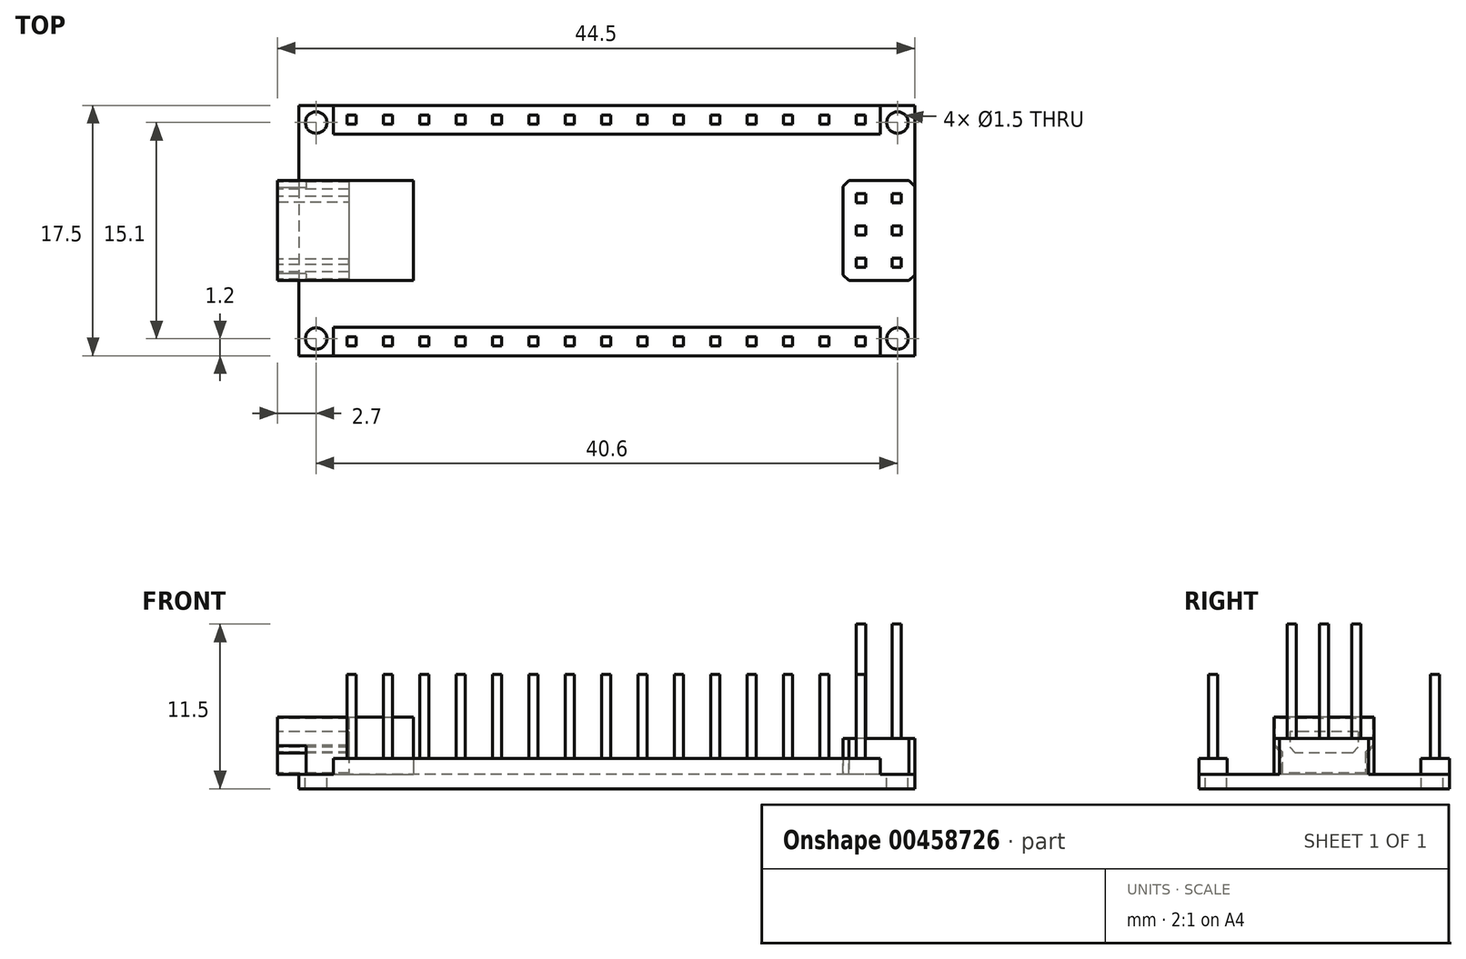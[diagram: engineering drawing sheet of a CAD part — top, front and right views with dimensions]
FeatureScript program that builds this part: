
annotation { "Feature Type Name" : "Feature", "Feature Type Description" : "" }
export const myFeature = defineFeature(function(context is Context, id is Id, definition is map)
    precondition{}
    {
        {
            var Q0;
            Q0=qCreatedBy(makeId("Top.planeOp"),FACE);
            var sketch = newSketch(context, id + "F0", { "sketchPlane" : qUnion([Q0])});
            skLineSegment(sketch, "E0.bottom", {"start": v(21.5, 8.75) * mm, "end": v(-21.5, 8.75) * mm});
            skLineSegment(sketch, "E0.top", {"start": v(21.5, -8.75) * mm, "end": v(-21.5, -8.75) * mm});
            skLineSegment(sketch, "E0.left", {"start": v(21.5, 8.75) * mm, "end": v(21.5, -8.75) * mm});
            skLineSegment(sketch, "E0.right", {"start": v(-21.5, 8.75) * mm, "end": v(-21.5, -8.75) * mm});
            skPoint(sketch, "E0.middle", {"position": v(0, 0) * mm});
            skCircle(sketch, "E1", {"center": v(-20.3, 7.55) * mm, "radius": 0.75 * mm});
            skCircle(sketch, "E2.0.1.0", {"center": v(-20.3, -7.55) * mm, "radius": 0.75 * mm});
            skCircle(sketch, "E2.1.0.0", {"center": v(20.3, 7.55) * mm, "radius": 0.75 * mm});
            skCircle(sketch, "E2.1.1.0", {"center": v(20.3, -7.55) * mm, "radius": 0.75 * mm});
            skLineSegment(sketch, "E2.direction1", {"start": v(-20.3, 7.55) * mm, "end": v(20.3, 7.55) * mm, "construction": true});
            skLineSegment(sketch, "E2.direction2", {"start": v(-20.3, 7.55) * mm, "end": v(-20.3, -7.55) * mm, "construction": true});
            skPoint(sketch, "E3", {"position": v(21.5, 0) * mm});
            skPoint(sketch, "E4", {"position": v(-21.5, 0) * mm});
            skLineSegment(sketch, "E5.bottom", {"start": v(-23, 3.5) * mm, "end": v(-13.5, 3.5) * mm});
            skLineSegment(sketch, "E5.top", {"start": v(-23, -3.5) * mm, "end": v(-13.5, -3.5) * mm});
            skLineSegment(sketch, "E5.left", {"start": v(-23, 3.5) * mm, "end": v(-23, -3.5) * mm});
            skLineSegment(sketch, "E5.right", {"start": v(-13.5, 3.5) * mm, "end": v(-13.5, -3.5) * mm});
            skPoint(sketch, "E6", {"position": v(-13.5, 0) * mm});
            skLineSegment(sketch, "E7.bottom", {"start": v(21.5, 3.5) * mm, "end": v(16.5, 3.5) * mm});
            skLineSegment(sketch, "E7.top", {"start": v(21.5, -3.5) * mm, "end": v(16.5, -3.5) * mm});
            skLineSegment(sketch, "E7.left", {"start": v(21.5, 3.5) * mm, "end": v(21.5, -3.5) * mm});
            skLineSegment(sketch, "E7.right", {"start": v(16.5, 3.5) * mm, "end": v(16.5, -3.5) * mm});
            skSolve(sketch);
        }
        {
            var Q0;
            {var subQ5=sQuery(id+"F0.wireOp",EDGE,"E5.right");Q0=makeQuery(id+"F0.imprint","IMPRINT",FACE,{"disambiguationData":[TD([[makeQuery(id+"F0.imprint","IMPRINT",EDGE,{"derivedFrom":subQ5}),-1.0]])]});}
            var Q1;
            {var subQ0=sQuery(id+"F0.wireOp",EDGE,"E0.bottom");Q1=makeQuery(id+"F0.imprint","IMPRINT",FACE,{"disambiguationData":[TD([[makeQuery(id+"F0.imprint","IMPRINT",EDGE,{"derivedFrom":subQ0}),1.0]])]});}
            var Q2;
            Q2=makeQuery(id+"F0.imprint","IMPRINT",FACE,{"disambiguationData":[TD([[makeQuery(id+"F0.imprint","IMPRINT",EDGE,{"derivedFrom":sQuery(id+"F0.wireOp",EDGE,"E7.bottom")}),1.0]])]});
            extrude(context, id + "F1", {"entities" : qUnion([Q0, Q1, Q2]), "oppositeDirection" : true, "depth" : 1 * mm});
        }
        {
            var Q0;
            {var subQ5=sQuery(id+"F0.wireOp",EDGE,"E5.left");Q0=makeQuery(id+"F0.imprint","IMPRINT",FACE,{"disambiguationData":[TD([[makeQuery(id+"F0.imprint","IMPRINT",EDGE,{"derivedFrom":subQ5}),1.0]])]});}
            var Q1;
            {var subQ5=sQuery(id+"F0.wireOp",EDGE,"E5.right");Q1=makeQuery(id+"F0.imprint","IMPRINT",FACE,{"disambiguationData":[TD([[makeQuery(id+"F0.imprint","IMPRINT",EDGE,{"derivedFrom":subQ5}),-1.0]])]});}
            extrude(context, id + "F2", {"entities" : qUnion([Q0, Q1]), "operationType" : NewBodyOperationType.ADD, "depth" : 4 * mm});
        }
        {
            var Q0;
            Q0=makeQuery(id+"F0.imprint","IMPRINT",FACE,{"disambiguationData":[TD([[makeQuery(id+"F0.imprint","IMPRINT",EDGE,{"derivedFrom":sQuery(id+"F0.wireOp",EDGE,"E7.bottom")}),1.0]])]});
            extrude(context, id + "F3", {"entities" : qUnion([Q0]), "operationType" : NewBodyOperationType.ADD, "depth" : 2.5 * mm});
        }
        {
            var Q0;
            Q0=makeQuery(id+"F2.opExtrude","SWEPT_FACE",FACE,{"disambiguationData":[OSD([sQuery(id+"F0.wireOp",EDGE,"E5.left")])]});
            var sketch = newSketch(context, id + "F4", { "sketchPlane" : qUnion([Q0])});
            skPoint(sketch, "E8", {"position": v(-3.5, 2) * mm});
            skPoint(sketch, "E9", {"position": v(3.5, 2) * mm});
            skPoint(sketch, "E10", {"position": v(-3, 0) * mm});
            skPoint(sketch, "E11", {"position": v(3, 0) * mm});
            skPoint(sketch, "E12", {"position": v(-3, 1.5) * mm});
            skPoint(sketch, "E13", {"position": v(3, 1.5) * mm});
            skLineSegment(sketch, "E14", {"start": v(-3.5, 2) * mm, "end": v(-3, 1.5) * mm});
            skLineSegment(sketch, "E15", {"start": v(-3, 0) * mm, "end": v(-3, 1.5) * mm});
            skLineSegment(sketch, "E16", {"start": v(3, 0) * mm, "end": v(3, 1.5) * mm});
            skLineSegment(sketch, "E17", {"start": v(3, 1.5) * mm, "end": v(3.5, 2) * mm});
            skLineSegment(sketch, "E18.bottom", {"start": v(-2.4, 3) * mm, "end": v(2.4, 3) * mm});
            skLineSegment(sketch, "E18.top", {"start": v(-2.4, 1.5) * mm, "end": v(2.4, 1.5) * mm});
            skLineSegment(sketch, "E18.left", {"start": v(-2.4, 3) * mm, "end": v(-2.4, 1.5) * mm});
            skLineSegment(sketch, "E18.right", {"start": v(2.4, 3) * mm, "end": v(2.4, 1.5) * mm});
            skPoint(sketch, "E19", {"position": v(0, 3) * mm});
            skPoint(sketch, "E20", {"position": v(-2.4, 2.25) * mm});
            skPoint(sketch, "E21", {"position": v(-3.5, 4) * mm});
            skPoint(sketch, "E22", {"position": v(3.5, 4) * mm});
            skLineSegment(sketch, "E23.0", {"start": v(-3.5, -1) * mm, "end": v(3.5, -1) * mm});
            skLineSegment(sketch, "E24", {"start": v(-3.5, 4) * mm, "end": v(-3.5, 2) * mm});
            skLineSegment(sketch, "E25", {"start": v(-3, 1.5) * mm, "end": v(-3, 0) * mm});
            skLineSegment(sketch, "E26", {"start": v(-3, 0) * mm, "end": v(3, 0) * mm});
            skLineSegment(sketch, "E27", {"start": v(3.5, 2) * mm, "end": v(3.5, 4) * mm});
            skLineSegment(sketch, "E28.0", {"start": v(-3.4, 3.9) * mm, "end": v(3.4, 3.9) * mm});
            skLineSegment(sketch, "E28.1", {"start": v(3.4, 2.04) * mm, "end": v(3.4, 3.9) * mm});
            skLineSegment(sketch, "E28.2", {"start": v(-3.4, 3.9) * mm, "end": v(-3.4, 2.04) * mm});
            skLineSegment(sketch, "E28.3", {"start": v(2.9, 1.54) * mm, "end": v(3.4, 2.04) * mm});
            skLineSegment(sketch, "E28.4", {"start": v(-3.4, 2.04) * mm, "end": v(-2.9, 1.54) * mm});
            skLineSegment(sketch, "E28.5", {"start": v(-2.9, 1.54) * mm, "end": v(-2.9, 0.1) * mm});
            skLineSegment(sketch, "E28.6", {"start": v(-2.9, 0.1) * mm, "end": v(2.9, 0.1) * mm});
            skLineSegment(sketch, "E28.7", {"start": v(2.9, 0.1) * mm, "end": v(2.9, 1.54) * mm});
            skPoint(sketch, "E29", {"position": v(-3.4, 2.04) * mm});
            skPoint(sketch, "E30", {"position": v(-2.9, 1.54) * mm});
            skSolve(sketch);
        }
        {
            var Q0;
            Q0=makeQuery(id+"F4.imprint","IMPRINT",FACE,{"disambiguationData":[TD([[makeQuery(id+"F4.imprint","IMPRINT",EDGE,{"derivedFrom":sQuery(id+"F4.wireOp",EDGE,"E18.bottom")}),1.0]])]});
            extrude(context, id + "F5", {"entities" : qUnion([Q0]), "operationType" : NewBodyOperationType.REMOVE, "oppositeDirection" : true, "depth" : 5 * mm});
        }
        {
            var Q0;
            {var subQ0=sQuery(id+"F4.wireOp",EDGE,"E14");Q0=makeQuery(id+"F4.imprint","IMPRINT",FACE,{"disambiguationData":[TD([[makeQuery(id+"F4.imprint","IMPRINT",EDGE,{"derivedFrom":subQ0}),-1.0]])]});}
            var Q1;
            {var subQ0=sQuery(id+"F4.wireOp",EDGE,"E16");Q1=makeQuery(id+"F4.imprint","IMPRINT",FACE,{"disambiguationData":[TD([[makeQuery(id+"F4.imprint","IMPRINT",EDGE,{"derivedFrom":subQ0}),-1.0]])]});}
            extrude(context, id + "F6", {"entities" : qUnion([Q0, Q1]), "operationType" : NewBodyOperationType.REMOVE, "oppositeDirection" : true, "depth" : 2 * mm});
        }
        {
            var Q0;
            Q0=makeQuery(id+"F1.opExtrude","CAP_FACE",FACE,{"disambiguationData":[OSD([sQuery(id+"F0.wireOp",EDGE,"E0.bottom"),sQuery(id+"F0.wireOp",EDGE,"E0.top"),sQuery(id+"F0.wireOp",EDGE,"E0.left"),sQuery(id+"F0.wireOp",EDGE,"E0.right"),sQuery(id+"F0.wireOp",EDGE,"E1"),sQuery(id+"F0.wireOp",EDGE,"E2.0.1.0"),sQuery(id+"F0.wireOp",EDGE,"E2.1.0.0"),sQuery(id+"F0.wireOp",EDGE,"E2.1.1.0"),sQuery(id+"F0.wireOp",EDGE,"E7.left")])],"isStart":false});
            var sketch = newSketch(context, id + "F7", { "sketchPlane" : qUnion([Q0])});
            skLineSegment(sketch, "E31.bottom", {"start": v(-19.1, 8.75) * mm, "end": v(19.1, 8.75) * mm});
            skLineSegment(sketch, "E31.top", {"start": v(-19.1, 6.75) * mm, "end": v(19.1, 6.75) * mm});
            skLineSegment(sketch, "E31.left", {"start": v(-19.1, 8.75) * mm, "end": v(-19.1, 6.75) * mm});
            skLineSegment(sketch, "E31.right", {"start": v(19.1, 8.75) * mm, "end": v(19.1, 6.75) * mm});
            skPoint(sketch, "E32", {"position": v(0, 6.75) * mm});
            skLineSegment(sketch, "E33", {"start": v(-19.1, 7.75) * mm, "end": v(19.1, 7.75) * mm, "construction": true});
            skPoint(sketch, "E34", {"position": v(-17.83, 7.75) * mm});
            skLineSegment(sketch, "E35.bottom", {"start": v(-17.51, 8.07) * mm, "end": v(-18.15, 8.07) * mm});
            skLineSegment(sketch, "E35.top", {"start": v(-17.51, 7.43) * mm, "end": v(-18.15, 7.43) * mm});
            skLineSegment(sketch, "E35.left", {"start": v(-17.51, 8.07) * mm, "end": v(-17.51, 7.43) * mm});
            skLineSegment(sketch, "E35.right", {"start": v(-18.15, 8.07) * mm, "end": v(-18.15, 7.43) * mm});
            skPoint(sketch, "E36.1.0.0", {"position": v(-15.3, 7.75) * mm});
            skLineSegment(sketch, "E36.1.0.1", {"start": v(-14.97, 8.07) * mm, "end": v(-14.97, 7.43) * mm});
            skLineSegment(sketch, "E36.1.0.2", {"start": v(-14.97, 8.07) * mm, "end": v(-15.61, 8.07) * mm});
            skLineSegment(sketch, "E36.1.0.3", {"start": v(-15.61, 8.07) * mm, "end": v(-15.61, 7.43) * mm});
            skLineSegment(sketch, "E36.1.0.4", {"start": v(-14.97, 7.43) * mm, "end": v(-15.61, 7.43) * mm});
            skPoint(sketch, "E36.2.0.0", {"position": v(-12.75, 7.75) * mm});
            skLineSegment(sketch, "E36.2.0.1", {"start": v(-12.43, 8.07) * mm, "end": v(-12.43, 7.43) * mm});
            skLineSegment(sketch, "E36.2.0.2", {"start": v(-12.43, 8.07) * mm, "end": v(-13.07, 8.07) * mm});
            skLineSegment(sketch, "E36.2.0.3", {"start": v(-13.07, 8.07) * mm, "end": v(-13.07, 7.43) * mm});
            skLineSegment(sketch, "E36.2.0.4", {"start": v(-12.43, 7.43) * mm, "end": v(-13.07, 7.43) * mm});
            skPoint(sketch, "E36.3.0.0", {"position": v(-10.21, 7.75) * mm});
            skLineSegment(sketch, "E36.3.0.1", {"start": v(-9.89, 8.07) * mm, "end": v(-9.89, 7.43) * mm});
            skLineSegment(sketch, "E36.3.0.2", {"start": v(-9.89, 8.07) * mm, "end": v(-10.53, 8.07) * mm});
            skLineSegment(sketch, "E36.3.0.3", {"start": v(-10.53, 8.07) * mm, "end": v(-10.53, 7.43) * mm});
            skLineSegment(sketch, "E36.3.0.4", {"start": v(-9.89, 7.43) * mm, "end": v(-10.53, 7.43) * mm});
            skPoint(sketch, "E36.4.0.0", {"position": v(-7.67, 7.75) * mm});
            skLineSegment(sketch, "E36.4.0.1", {"start": v(-7.35, 8.07) * mm, "end": v(-7.35, 7.43) * mm});
            skLineSegment(sketch, "E36.4.0.2", {"start": v(-7.35, 8.07) * mm, "end": v(-8, 8.07) * mm});
            skLineSegment(sketch, "E36.4.0.3", {"start": v(-8, 8.07) * mm, "end": v(-8, 7.43) * mm});
            skLineSegment(sketch, "E36.4.0.4", {"start": v(-7.35, 7.43) * mm, "end": v(-8, 7.43) * mm});
            skPoint(sketch, "E36.5.0.0", {"position": v(-5.13, 7.75) * mm});
            skLineSegment(sketch, "E36.5.0.1", {"start": v(-4.8, 8.07) * mm, "end": v(-4.8, 7.43) * mm});
            skLineSegment(sketch, "E36.5.0.2", {"start": v(-4.8, 8.07) * mm, "end": v(-5.45, 8.07) * mm});
            skLineSegment(sketch, "E36.5.0.3", {"start": v(-5.45, 8.07) * mm, "end": v(-5.45, 7.43) * mm});
            skLineSegment(sketch, "E36.5.0.4", {"start": v(-4.8, 7.43) * mm, "end": v(-5.45, 7.43) * mm});
            skPoint(sketch, "E36.6.0.0", {"position": v(-2.59, 7.75) * mm});
            skLineSegment(sketch, "E36.6.0.1", {"start": v(-2.27, 8.07) * mm, "end": v(-2.27, 7.43) * mm});
            skLineSegment(sketch, "E36.6.0.2", {"start": v(-2.27, 8.07) * mm, "end": v(-2.9, 8.07) * mm});
            skLineSegment(sketch, "E36.6.0.3", {"start": v(-2.9, 8.07) * mm, "end": v(-2.9, 7.43) * mm});
            skLineSegment(sketch, "E36.6.0.4", {"start": v(-2.27, 7.43) * mm, "end": v(-2.9, 7.43) * mm});
            skPoint(sketch, "E36.7.0.0", {"position": v(-0.05, 7.75) * mm});
            skLineSegment(sketch, "E36.7.0.1", {"start": v(0.27, 8.07) * mm, "end": v(0.27, 7.43) * mm});
            skLineSegment(sketch, "E36.7.0.2", {"start": v(0.27, 8.07) * mm, "end": v(-0.37, 8.07) * mm});
            skLineSegment(sketch, "E36.7.0.3", {"start": v(-0.37, 8.07) * mm, "end": v(-0.37, 7.43) * mm});
            skLineSegment(sketch, "E36.7.0.4", {"start": v(0.27, 7.43) * mm, "end": v(-0.37, 7.43) * mm});
            skPoint(sketch, "E36.8.0.0", {"position": v(2.5, 7.75) * mm});
            skLineSegment(sketch, "E36.8.0.1", {"start": v(2.81, 8.07) * mm, "end": v(2.81, 7.43) * mm});
            skLineSegment(sketch, "E36.8.0.2", {"start": v(2.81, 8.07) * mm, "end": v(2.17, 8.07) * mm});
            skLineSegment(sketch, "E36.8.0.3", {"start": v(2.17, 8.07) * mm, "end": v(2.17, 7.43) * mm});
            skLineSegment(sketch, "E36.8.0.4", {"start": v(2.81, 7.43) * mm, "end": v(2.17, 7.43) * mm});
            skPoint(sketch, "E36.9.0.0", {"position": v(5.03, 7.75) * mm});
            skLineSegment(sketch, "E36.9.0.1", {"start": v(5.35, 8.07) * mm, "end": v(5.35, 7.43) * mm});
            skLineSegment(sketch, "E36.9.0.2", {"start": v(5.35, 8.07) * mm, "end": v(4.71, 8.07) * mm});
            skLineSegment(sketch, "E36.9.0.3", {"start": v(4.71, 8.07) * mm, "end": v(4.71, 7.43) * mm});
            skLineSegment(sketch, "E36.9.0.4", {"start": v(5.35, 7.43) * mm, "end": v(4.71, 7.43) * mm});
            skPoint(sketch, "E36.10.0.0", {"position": v(7.57, 7.75) * mm});
            skLineSegment(sketch, "E36.10.0.1", {"start": v(7.9, 8.07) * mm, "end": v(7.9, 7.43) * mm});
            skLineSegment(sketch, "E36.10.0.2", {"start": v(7.9, 8.07) * mm, "end": v(7.25, 8.07) * mm});
            skLineSegment(sketch, "E36.10.0.3", {"start": v(7.25, 8.07) * mm, "end": v(7.25, 7.43) * mm});
            skLineSegment(sketch, "E36.10.0.4", {"start": v(7.9, 7.43) * mm, "end": v(7.25, 7.43) * mm});
            skPoint(sketch, "E36.11.0.0", {"position": v(10.11, 7.75) * mm});
            skLineSegment(sketch, "E36.11.0.1", {"start": v(10.43, 8.07) * mm, "end": v(10.43, 7.43) * mm});
            skLineSegment(sketch, "E36.11.0.2", {"start": v(10.43, 8.07) * mm, "end": v(9.8, 8.07) * mm});
            skLineSegment(sketch, "E36.11.0.3", {"start": v(9.8, 8.07) * mm, "end": v(9.8, 7.43) * mm});
            skLineSegment(sketch, "E36.11.0.4", {"start": v(10.43, 7.43) * mm, "end": v(9.8, 7.43) * mm});
            skPoint(sketch, "E36.12.0.0", {"position": v(12.65, 7.75) * mm});
            skLineSegment(sketch, "E36.12.0.1", {"start": v(12.97, 8.07) * mm, "end": v(12.97, 7.43) * mm});
            skLineSegment(sketch, "E36.12.0.2", {"start": v(12.97, 8.07) * mm, "end": v(12.33, 8.07) * mm});
            skLineSegment(sketch, "E36.12.0.3", {"start": v(12.33, 8.07) * mm, "end": v(12.33, 7.43) * mm});
            skLineSegment(sketch, "E36.12.0.4", {"start": v(12.97, 7.43) * mm, "end": v(12.33, 7.43) * mm});
            skPoint(sketch, "E36.13.0.0", {"position": v(15.2, 7.75) * mm});
            skLineSegment(sketch, "E36.13.0.1", {"start": v(15.51, 8.07) * mm, "end": v(15.51, 7.43) * mm});
            skLineSegment(sketch, "E36.13.0.2", {"start": v(15.51, 8.07) * mm, "end": v(14.87, 8.07) * mm});
            skLineSegment(sketch, "E36.13.0.3", {"start": v(14.87, 8.07) * mm, "end": v(14.87, 7.43) * mm});
            skLineSegment(sketch, "E36.13.0.4", {"start": v(15.51, 7.43) * mm, "end": v(14.87, 7.43) * mm});
            skPoint(sketch, "E36.14.0.0", {"position": v(17.73, 7.75) * mm});
            skLineSegment(sketch, "E36.14.0.1", {"start": v(18.05, 8.07) * mm, "end": v(18.05, 7.43) * mm});
            skLineSegment(sketch, "E36.14.0.2", {"start": v(18.05, 8.07) * mm, "end": v(17.41, 8.07) * mm});
            skLineSegment(sketch, "E36.14.0.3", {"start": v(17.41, 8.07) * mm, "end": v(17.41, 7.43) * mm});
            skLineSegment(sketch, "E36.14.0.4", {"start": v(18.05, 7.43) * mm, "end": v(17.41, 7.43) * mm});
            skLineSegment(sketch, "E36.direction1", {"start": v(-17.83, 7.75) * mm, "end": v(-15.3, 7.75) * mm, "construction": true});
            skPoint(sketch, "E37", {"position": v(-20.3, 7.55) * mm});
            skLineSegment(sketch, "E38", {"start": v(-20.3, 7.55) * mm, "end": v(-21.5, 7.55) * mm});
            skLineSegment(sketch, "E39", {"start": v(-21.5, 7.55) * mm, "end": v(-19.1, 7.55) * mm});
            skPoint(sketch, "E40", {"position": v(-21.05, 7.55) * mm});
            skPoint(sketch, "E41", {"position": v(-19.55, 7.55) * mm});
            skPoint(sketch, "E42", {"position": v(20.3, 7.55) * mm});
            skLineSegment(sketch, "E43", {"start": v(20.3, 7.55) * mm, "end": v(21.5, 7.55) * mm});
            skLineSegment(sketch, "E44", {"start": v(21.5, 7.55) * mm, "end": v(19.1, 7.55) * mm});
            skPoint(sketch, "E45", {"position": v(21.05, 7.55) * mm});
            skPoint(sketch, "E46", {"position": v(19.55, 7.55) * mm});
            skPoint(sketch, "E47.0.1.0", {"position": v(-0.05, -7.75) * mm});
            skPoint(sketch, "E47.0.1.1", {"position": v(-5.13, -7.75) * mm});
            skPoint(sketch, "E47.0.1.2", {"position": v(12.65, -7.75) * mm});
            skPoint(sketch, "E47.0.1.3", {"position": v(-7.67, -7.75) * mm});
            skPoint(sketch, "E47.0.1.4", {"position": v(17.73, -7.75) * mm});
            skPoint(sketch, "E47.0.1.5", {"position": v(-10.21, -7.75) * mm});
            skPoint(sketch, "E47.0.1.6", {"position": v(7.57, -7.75) * mm});
            skPoint(sketch, "E47.0.1.7", {"position": v(2.49, -7.75) * mm});
            skPoint(sketch, "E47.0.1.8", {"position": v(0, -8.75) * mm});
            skPoint(sketch, "E47.0.1.9", {"position": v(-17.83, -7.75) * mm});
            skPoint(sketch, "E47.0.1.10", {"position": v(5.03, -7.75) * mm});
            skPoint(sketch, "E47.0.1.11", {"position": v(-15.3, -7.75) * mm});
            skLineSegment(sketch, "E47.0.1.12", {"start": v(-17.83, -7.75) * mm, "end": v(-15.3, -7.75) * mm, "construction": true});
            skPoint(sketch, "E47.0.1.13", {"position": v(10.11, -7.75) * mm});
            skPoint(sketch, "E47.0.1.14", {"position": v(15.2, -7.75) * mm});
            skPoint(sketch, "E47.0.1.15", {"position": v(-2.6, -7.75) * mm});
            skPoint(sketch, "E47.0.1.16", {"position": v(-12.75, -7.75) * mm});
            skPoint(sketch, "E47.0.1.17", {"position": v(-17.83, -7.75) * mm});
            skLineSegment(sketch, "E47.0.1.18", {"start": v(18.05, -7.43) * mm, "end": v(17.41, -7.43) * mm});
            skLineSegment(sketch, "E47.0.1.19", {"start": v(18.05, -8.07) * mm, "end": v(17.41, -8.07) * mm});
            skLineSegment(sketch, "E47.0.1.20", {"start": v(18.05, -7.43) * mm, "end": v(18.05, -8.07) * mm});
            skLineSegment(sketch, "E47.0.1.21", {"start": v(-0.37, -7.43) * mm, "end": v(-0.37, -8.07) * mm});
            skLineSegment(sketch, "E47.0.1.22", {"start": v(-10.53, -7.43) * mm, "end": v(-10.53, -8.07) * mm});
            skLineSegment(sketch, "E47.0.1.23", {"start": v(-9.89, -7.43) * mm, "end": v(-10.53, -7.43) * mm});
            skLineSegment(sketch, "E47.0.1.24", {"start": v(-2.27, -7.43) * mm, "end": v(-2.9, -7.43) * mm});
            skLineSegment(sketch, "E47.0.1.25", {"start": v(12.97, -7.43) * mm, "end": v(12.97, -8.07) * mm});
            skLineSegment(sketch, "E47.0.1.26", {"start": v(-5.45, -7.43) * mm, "end": v(-5.45, -8.07) * mm});
            skLineSegment(sketch, "E47.0.1.27", {"start": v(-7.35, -8.07) * mm, "end": v(-7.99, -8.07) * mm});
            skLineSegment(sketch, "E47.0.1.28", {"start": v(2.81, -8.07) * mm, "end": v(2.17, -8.07) * mm});
            skLineSegment(sketch, "E47.0.1.29", {"start": v(12.97, -8.07) * mm, "end": v(12.33, -8.07) * mm});
            skLineSegment(sketch, "E47.0.1.30", {"start": v(7.9, -8.07) * mm, "end": v(7.25, -8.07) * mm});
            skLineSegment(sketch, "E47.0.1.31", {"start": v(7.25, -7.43) * mm, "end": v(7.25, -8.07) * mm});
            skLineSegment(sketch, "E47.0.1.32", {"start": v(-2.9, -7.43) * mm, "end": v(-2.9, -8.07) * mm});
            skLineSegment(sketch, "E47.0.1.33", {"start": v(-7.35, -7.43) * mm, "end": v(-7.99, -7.43) * mm});
            skLineSegment(sketch, "E47.0.1.34", {"start": v(2.81, -7.43) * mm, "end": v(2.81, -8.07) * mm});
            skLineSegment(sketch, "E47.0.1.35", {"start": v(7.9, -7.43) * mm, "end": v(7.25, -7.43) * mm});
            skLineSegment(sketch, "E47.0.1.36", {"start": v(-4.8, -8.07) * mm, "end": v(-5.45, -8.07) * mm});
            skLineSegment(sketch, "E47.0.1.37", {"start": v(-7.35, -7.43) * mm, "end": v(-7.35, -8.07) * mm});
            skLineSegment(sketch, "E47.0.1.38", {"start": v(15.5, -8.07) * mm, "end": v(14.87, -8.07) * mm});
            skLineSegment(sketch, "E47.0.1.39", {"start": v(5.35, -8.07) * mm, "end": v(4.71, -8.07) * mm});
            skLineSegment(sketch, "E47.0.1.40", {"start": v(-2.27, -8.07) * mm, "end": v(-2.9, -8.07) * mm});
            skLineSegment(sketch, "E47.0.1.41", {"start": v(-12.43, -8.07) * mm, "end": v(-13.07, -8.07) * mm});
            skLineSegment(sketch, "E47.0.1.42", {"start": v(2.81, -7.43) * mm, "end": v(2.17, -7.43) * mm});
            skLineSegment(sketch, "E47.0.1.43", {"start": v(17.41, -7.43) * mm, "end": v(17.41, -8.07) * mm});
            skLineSegment(sketch, "E47.0.1.44", {"start": v(12.97, -7.43) * mm, "end": v(12.33, -7.43) * mm});
            skLineSegment(sketch, "E47.0.1.45", {"start": v(7.9, -7.43) * mm, "end": v(7.9, -8.07) * mm});
            skLineSegment(sketch, "E47.0.1.46", {"start": v(-2.27, -7.43) * mm, "end": v(-2.27, -8.07) * mm});
            skLineSegment(sketch, "E47.0.1.47", {"start": v(-17.5, -8.07) * mm, "end": v(-18.15, -8.07) * mm});
            skLineSegment(sketch, "E47.0.1.48", {"start": v(12.33, -7.43) * mm, "end": v(12.33, -8.07) * mm});
            skLineSegment(sketch, "E47.0.1.49", {"start": v(-14.97, -7.43) * mm, "end": v(-14.97, -8.07) * mm});
            skLineSegment(sketch, "E47.0.1.50", {"start": v(2.17, -7.43) * mm, "end": v(2.17, -8.07) * mm});
            skLineSegment(sketch, "E47.0.1.51", {"start": v(-8, -7.43) * mm, "end": v(-8, -8.07) * mm});
            skLineSegment(sketch, "E47.0.1.52", {"start": v(-14.97, -7.43) * mm, "end": v(-15.6, -7.43) * mm});
            skLineSegment(sketch, "E47.0.1.53", {"start": v(-15.61, -7.43) * mm, "end": v(-15.61, -8.07) * mm});
            skLineSegment(sketch, "E47.0.1.54", {"start": v(-14.97, -8.07) * mm, "end": v(-15.6, -8.07) * mm});
            skLineSegment(sketch, "E47.0.1.55", {"start": v(-9.89, -7.43) * mm, "end": v(-9.89, -8.07) * mm});
            skLineSegment(sketch, "E47.0.1.56", {"start": v(0.27, -7.43) * mm, "end": v(0.27, -8.07) * mm});
            skLineSegment(sketch, "E47.0.1.57", {"start": v(10.43, -7.43) * mm, "end": v(10.43, -8.07) * mm});
            skLineSegment(sketch, "E47.0.1.58", {"start": v(-12.43, -7.43) * mm, "end": v(-12.43, -8.07) * mm});
            skLineSegment(sketch, "E47.0.1.59", {"start": v(10.43, -7.43) * mm, "end": v(9.8, -7.43) * mm});
            skLineSegment(sketch, "E47.0.1.60", {"start": v(0.27, -7.43) * mm, "end": v(-0.37, -7.43) * mm});
            skLineSegment(sketch, "E47.0.1.61", {"start": v(15.51, -7.43) * mm, "end": v(15.51, -8.07) * mm});
            skLineSegment(sketch, "E47.0.1.62", {"start": v(5.35, -7.43) * mm, "end": v(5.35, -8.07) * mm});
            skLineSegment(sketch, "E47.0.1.63", {"start": v(-4.8, -7.43) * mm, "end": v(-4.8, -8.07) * mm});
            skLineSegment(sketch, "E47.0.1.64", {"start": v(15.51, -7.43) * mm, "end": v(14.87, -7.43) * mm});
            skLineSegment(sketch, "E47.0.1.65", {"start": v(5.35, -7.43) * mm, "end": v(4.71, -7.43) * mm});
            skLineSegment(sketch, "E47.0.1.66", {"start": v(-4.8, -7.43) * mm, "end": v(-5.45, -7.43) * mm});
            skLineSegment(sketch, "E47.0.1.67", {"start": v(10.43, -8.07) * mm, "end": v(9.8, -8.07) * mm});
            skLineSegment(sketch, "E47.0.1.68", {"start": v(0.27, -8.07) * mm, "end": v(-0.37, -8.07) * mm});
            skLineSegment(sketch, "E47.0.1.69", {"start": v(-9.9, -8.07) * mm, "end": v(-10.53, -8.07) * mm});
            skLineSegment(sketch, "E47.0.1.70", {"start": v(4.71, -7.43) * mm, "end": v(4.71, -8.07) * mm});
            skLineSegment(sketch, "E47.0.1.71", {"start": v(14.87, -7.43) * mm, "end": v(14.87, -8.07) * mm});
            skLineSegment(sketch, "E47.0.1.72", {"start": v(9.8, -7.43) * mm, "end": v(9.8, -8.07) * mm});
            skLineSegment(sketch, "E47.0.1.73", {"start": v(-12.43, -7.43) * mm, "end": v(-13.07, -7.43) * mm});
            skLineSegment(sketch, "E47.0.1.74", {"start": v(-13.07, -7.43) * mm, "end": v(-13.07, -8.07) * mm});
            skLineSegment(sketch, "E47.0.1.75", {"start": v(-18.15, -7.43) * mm, "end": v(-18.15, -8.07) * mm});
            skLineSegment(sketch, "E47.0.1.76", {"start": v(-17.51, -7.43) * mm, "end": v(-17.51, -8.07) * mm});
            skLineSegment(sketch, "E47.0.1.77", {"start": v(-17.5, -7.43) * mm, "end": v(-18.15, -7.43) * mm});
            skLineSegment(sketch, "E47.0.1.78", {"start": v(19.1, -6.75) * mm, "end": v(19.1, -8.75) * mm});
            skLineSegment(sketch, "E47.0.1.79", {"start": v(-19.1, -8.75) * mm, "end": v(19.1, -8.75) * mm});
            skLineSegment(sketch, "E47.0.1.80", {"start": v(-19.1, -6.75) * mm, "end": v(-19.1, -8.75) * mm});
            skLineSegment(sketch, "E47.0.1.81", {"start": v(-19.1, -6.75) * mm, "end": v(19.1, -6.75) * mm});
            skLineSegment(sketch, "E47.direction1", {"start": v(-0.05, 7.75) * mm, "end": v(24.95, 7.75) * mm, "construction": true});
            skLineSegment(sketch, "E47.direction2", {"start": v(-0.05, 7.75) * mm, "end": v(-0.05, -7.75) * mm, "construction": true});
            skSolve(sketch);
        }
        {
            var Q0;
            Q0=makeQuery(id+"F7.imprint","IMPRINT",FACE,{"disambiguationData":[TD([[makeQuery(id+"F7.imprint","IMPRINT",EDGE,{"derivedFrom":sQuery(id+"F7.wireOp",EDGE,"E47.0.1.18")}),-1.0]])]});
            var Q1;
            {var subQ1=sQuery(id+"F7.wireOp",EDGE,"E31.bottom");Q1=makeQuery(id+"F7.imprint","IMPRINT",FACE,{"disambiguationData":[TD([[makeQuery(id+"F7.imprint","IMPRINT",EDGE,{"derivedFrom":subQ1}),1.0]])]});}
            extrude(context, id + "F8", {"entities" : qUnion([Q0, Q1]), "oppositeDirection" : true, "depth" : 2.1 * mm, "offsetDistance" : 25 * mm});
        }
        {
            var Q0;
            Q0=makeQuery(id+"F7.imprint","IMPRINT",FACE,{"disambiguationData":[TD([[makeQuery(id+"F7.imprint","IMPRINT",EDGE,{"derivedFrom":sQuery(id+"F7.wireOp",EDGE,"E35.bottom")}),1.0]])]});
            var Q1;
            Q1=makeQuery(id+"F7.imprint","IMPRINT",FACE,{"disambiguationData":[TD([[makeQuery(id+"F7.imprint","IMPRINT",EDGE,{"derivedFrom":sQuery(id+"F7.wireOp",EDGE,"E36.1.0.1")}),-1.0]])]});
            var Q2;
            Q2=makeQuery(id+"F7.imprint","IMPRINT",FACE,{"disambiguationData":[TD([[makeQuery(id+"F7.imprint","IMPRINT",EDGE,{"derivedFrom":sQuery(id+"F7.wireOp",EDGE,"E36.2.0.1")}),-1.0]])]});
            var Q3;
            Q3=makeQuery(id+"F7.imprint","IMPRINT",FACE,{"disambiguationData":[TD([[makeQuery(id+"F7.imprint","IMPRINT",EDGE,{"derivedFrom":sQuery(id+"F7.wireOp",EDGE,"E36.3.0.1")}),-1.0]])]});
            var Q4;
            Q4=makeQuery(id+"F7.imprint","IMPRINT",FACE,{"disambiguationData":[TD([[makeQuery(id+"F7.imprint","IMPRINT",EDGE,{"derivedFrom":sQuery(id+"F7.wireOp",EDGE,"E36.4.0.1")}),-1.0]])]});
            var Q5;
            Q5=makeQuery(id+"F7.imprint","IMPRINT",FACE,{"disambiguationData":[TD([[makeQuery(id+"F7.imprint","IMPRINT",EDGE,{"derivedFrom":sQuery(id+"F7.wireOp",EDGE,"E36.5.0.1")}),-1.0]])]});
            var Q6;
            Q6=makeQuery(id+"F7.imprint","IMPRINT",FACE,{"disambiguationData":[TD([[makeQuery(id+"F7.imprint","IMPRINT",EDGE,{"derivedFrom":sQuery(id+"F7.wireOp",EDGE,"E36.6.0.1")}),-1.0]])]});
            var Q7;
            Q7=makeQuery(id+"F7.imprint","IMPRINT",FACE,{"disambiguationData":[TD([[makeQuery(id+"F7.imprint","IMPRINT",EDGE,{"derivedFrom":sQuery(id+"F7.wireOp",EDGE,"E36.7.0.1")}),-1.0]])]});
            var Q8;
            Q8=makeQuery(id+"F7.imprint","IMPRINT",FACE,{"disambiguationData":[TD([[makeQuery(id+"F7.imprint","IMPRINT",EDGE,{"derivedFrom":sQuery(id+"F7.wireOp",EDGE,"E36.8.0.1")}),-1.0]])]});
            var Q9;
            Q9=makeQuery(id+"F7.imprint","IMPRINT",FACE,{"disambiguationData":[TD([[makeQuery(id+"F7.imprint","IMPRINT",EDGE,{"derivedFrom":sQuery(id+"F7.wireOp",EDGE,"E36.9.0.1")}),-1.0]])]});
            var Q10;
            Q10=makeQuery(id+"F7.imprint","IMPRINT",FACE,{"disambiguationData":[TD([[makeQuery(id+"F7.imprint","IMPRINT",EDGE,{"derivedFrom":sQuery(id+"F7.wireOp",EDGE,"E36.10.0.1")}),-1.0]])]});
            var Q11;
            Q11=makeQuery(id+"F7.imprint","IMPRINT",FACE,{"disambiguationData":[TD([[makeQuery(id+"F7.imprint","IMPRINT",EDGE,{"derivedFrom":sQuery(id+"F7.wireOp",EDGE,"E36.11.0.1")}),-1.0]])]});
            var Q12;
            Q12=makeQuery(id+"F7.imprint","IMPRINT",FACE,{"disambiguationData":[TD([[makeQuery(id+"F7.imprint","IMPRINT",EDGE,{"derivedFrom":sQuery(id+"F7.wireOp",EDGE,"E36.12.0.1")}),-1.0]])]});
            var Q13;
            Q13=makeQuery(id+"F7.imprint","IMPRINT",FACE,{"disambiguationData":[TD([[makeQuery(id+"F7.imprint","IMPRINT",EDGE,{"derivedFrom":sQuery(id+"F7.wireOp",EDGE,"E36.13.0.1")}),-1.0]])]});
            var Q14;
            Q14=makeQuery(id+"F7.imprint","IMPRINT",FACE,{"disambiguationData":[TD([[makeQuery(id+"F7.imprint","IMPRINT",EDGE,{"derivedFrom":sQuery(id+"F7.wireOp",EDGE,"E36.14.0.1")}),-1.0]])]});
            var Q15;
            Q15=makeQuery(id+"F7.imprint","IMPRINT",FACE,{"disambiguationData":[TD([[makeQuery(id+"F7.imprint","IMPRINT",EDGE,{"derivedFrom":sQuery(id+"F7.wireOp",EDGE,"E47.0.1.47")}),-1.0]])]});
            var Q16;
            Q16=makeQuery(id+"F7.imprint","IMPRINT",FACE,{"disambiguationData":[TD([[makeQuery(id+"F7.imprint","IMPRINT",EDGE,{"derivedFrom":sQuery(id+"F7.wireOp",EDGE,"E47.0.1.49")}),-1.0]])]});
            var Q17;
            Q17=makeQuery(id+"F7.imprint","IMPRINT",FACE,{"disambiguationData":[TD([[makeQuery(id+"F7.imprint","IMPRINT",EDGE,{"derivedFrom":sQuery(id+"F7.wireOp",EDGE,"E47.0.1.41")}),-1.0]])]});
            var Q18;
            Q18=makeQuery(id+"F7.imprint","IMPRINT",FACE,{"disambiguationData":[TD([[makeQuery(id+"F7.imprint","IMPRINT",EDGE,{"derivedFrom":sQuery(id+"F7.wireOp",EDGE,"E47.0.1.22")}),1.0]])]});
            var Q19;
            Q19=makeQuery(id+"F7.imprint","IMPRINT",FACE,{"disambiguationData":[TD([[makeQuery(id+"F7.imprint","IMPRINT",EDGE,{"derivedFrom":sQuery(id+"F7.wireOp",EDGE,"E47.0.1.27")}),-1.0]])]});
            var Q20;
            Q20=makeQuery(id+"F7.imprint","IMPRINT",FACE,{"disambiguationData":[TD([[makeQuery(id+"F7.imprint","IMPRINT",EDGE,{"derivedFrom":sQuery(id+"F7.wireOp",EDGE,"E47.0.1.26")}),1.0]])]});
            var Q21;
            Q21=makeQuery(id+"F7.imprint","IMPRINT",FACE,{"disambiguationData":[TD([[makeQuery(id+"F7.imprint","IMPRINT",EDGE,{"derivedFrom":sQuery(id+"F7.wireOp",EDGE,"E47.0.1.24")}),1.0]])]});
            var Q22;
            Q22=makeQuery(id+"F7.imprint","IMPRINT",FACE,{"disambiguationData":[TD([[makeQuery(id+"F7.imprint","IMPRINT",EDGE,{"derivedFrom":sQuery(id+"F7.wireOp",EDGE,"E47.0.1.21")}),1.0]])]});
            var Q23;
            Q23=makeQuery(id+"F7.imprint","IMPRINT",FACE,{"disambiguationData":[TD([[makeQuery(id+"F7.imprint","IMPRINT",EDGE,{"derivedFrom":sQuery(id+"F7.wireOp",EDGE,"E47.0.1.28")}),-1.0]])]});
            var Q24;
            Q24=makeQuery(id+"F7.imprint","IMPRINT",FACE,{"disambiguationData":[TD([[makeQuery(id+"F7.imprint","IMPRINT",EDGE,{"derivedFrom":sQuery(id+"F7.wireOp",EDGE,"E47.0.1.39")}),-1.0]])]});
            var Q25;
            Q25=makeQuery(id+"F7.imprint","IMPRINT",FACE,{"disambiguationData":[TD([[makeQuery(id+"F7.imprint","IMPRINT",EDGE,{"derivedFrom":sQuery(id+"F7.wireOp",EDGE,"E47.0.1.30")}),-1.0]])]});
            var Q26;
            Q26=makeQuery(id+"F7.imprint","IMPRINT",FACE,{"disambiguationData":[TD([[makeQuery(id+"F7.imprint","IMPRINT",EDGE,{"derivedFrom":sQuery(id+"F7.wireOp",EDGE,"E47.0.1.57")}),-1.0]])]});
            var Q27;
            Q27=makeQuery(id+"F7.imprint","IMPRINT",FACE,{"disambiguationData":[TD([[makeQuery(id+"F7.imprint","IMPRINT",EDGE,{"derivedFrom":sQuery(id+"F7.wireOp",EDGE,"E47.0.1.25")}),-1.0]])]});
            var Q28;
            Q28=makeQuery(id+"F7.imprint","IMPRINT",FACE,{"disambiguationData":[TD([[makeQuery(id+"F7.imprint","IMPRINT",EDGE,{"derivedFrom":sQuery(id+"F7.wireOp",EDGE,"E47.0.1.38")}),-1.0]])]});
            var Q29;
            Q29=makeQuery(id+"F7.imprint","IMPRINT",FACE,{"disambiguationData":[TD([[makeQuery(id+"F7.imprint","IMPRINT",EDGE,{"derivedFrom":sQuery(id+"F7.wireOp",EDGE,"E47.0.1.18")}),1.0]])]});
            extrude(context, id + "F9", {"entities" : qUnion([Q0, Q1, Q2, Q3, Q4, Q5, Q6, Q7, Q8, Q9, Q10, Q11, Q12, Q13, Q14, Q15, Q16, Q17, Q18, Q19, Q20, Q21, Q22, Q23, Q24, Q25, Q26, Q27, Q28, Q29]), "operationType" : NewBodyOperationType.ADD, "oppositeDirection" : true, "depth" : 8 * mm, "offsetDistance" : 25 * mm});
        }
        {
            var Q0;
            Q0=makeQuery(id+"F5.boolean.opBoolean","COPY",EDGE,{"derivedFrom":makeQuery(id+"F5.opExtrude","SWEPT_EDGE",EDGE,{"disambiguationData":[OSD([sQuery(id+"F4.wireOp",EDGE,"E18.top"),sQuery(id+"F4.wireOp",EDGE,"E18.right")])]})});
            var Q1;
            Q1=makeQuery(id+"F5.boolean.opBoolean","COPY",EDGE,{"derivedFrom":makeQuery(id+"F5.opExtrude","SWEPT_EDGE",EDGE,{"disambiguationData":[OSD([sQuery(id+"F4.wireOp",EDGE,"E18.top"),sQuery(id+"F4.wireOp",EDGE,"E18.left")])]})});
            chamfer(context, id + "F10", {"entities" : qUnion([Q0, Q1]), "width" : 0.4 * mm, "tangentPropagation" : true});
        }
        {
            var Q0;
            Q0=makeQuery(id+"F3.opExtrude","CAP_FACE",FACE,{"disambiguationData":[OSD([sQuery(id+"F0.wireOp",EDGE,"E7.bottom"),sQuery(id+"F0.wireOp",EDGE,"E7.top"),sQuery(id+"F0.wireOp",EDGE,"E7.left"),sQuery(id+"F0.wireOp",EDGE,"E7.right")])],"isStart":false});
            var sketch = newSketch(context, id + "F11", { "sketchPlane" : qUnion([Q0])});
            skPoint(sketch, "E48", {"position": v(21.5, 1.17) * mm});
            skPoint(sketch, "E49", {"position": v(21.5, -1.17) * mm});
            skLineSegment(sketch, "E50", {"start": v(21.5, 3.5) * mm, "end": v(21.5, 1.17) * mm});
            skLineSegment(sketch, "E51", {"start": v(21.5, -1.17) * mm, "end": v(21.5, 1.17) * mm});
            skLineSegment(sketch, "E52", {"start": v(21.5, -1.17) * mm, "end": v(21.5, -3.5) * mm});
            skLineSegment(sketch, "E53", {"start": v(21.5, 1.17) * mm, "end": v(16.5, 1.17) * mm});
            skLineSegment(sketch, "E54", {"start": v(21.5, -1.17) * mm, "end": v(16.5, -1.17) * mm});
            skPoint(sketch, "E55", {"position": v(19, 3.5) * mm});
            skPoint(sketch, "E56", {"position": v(19, -3.5) * mm});
            skLineSegment(sketch, "E57", {"start": v(19, 3.5) * mm, "end": v(19, -3.5) * mm});
            skPoint(sketch, "E58", {"position": v(17.75, 2.25) * mm});
            skLineSegment(sketch, "E59", {"start": v(17.75, 2.25) * mm, "end": v(17.75, 3.5) * mm, "construction": true});
            skLineSegment(sketch, "E60", {"start": v(17.75, 2.25) * mm, "end": v(16.5, 2.25) * mm, "construction": true});
            skLineSegment(sketch, "E61", {"start": v(17.75, 2.25) * mm, "end": v(19, 2.25) * mm, "construction": true});
            skLineSegment(sketch, "E62", {"start": v(17.75, 2.25) * mm, "end": v(17.75, 1.17) * mm, "construction": true});
            skLineSegment(sketch, "E63.bottom", {"start": v(18.07, 2.57) * mm, "end": v(17.43, 2.57) * mm});
            skLineSegment(sketch, "E63.top", {"start": v(18.07, 1.93) * mm, "end": v(17.43, 1.93) * mm});
            skLineSegment(sketch, "E63.left", {"start": v(18.07, 2.57) * mm, "end": v(18.07, 1.93) * mm});
            skLineSegment(sketch, "E63.right", {"start": v(17.43, 2.57) * mm, "end": v(17.43, 1.93) * mm});
            skLineSegment(sketch, "E64.1.0.0", {"start": v(20.57, 2.57) * mm, "end": v(20.57, 1.93) * mm});
            skLineSegment(sketch, "E64.1.0.1", {"start": v(20.57, 2.57) * mm, "end": v(19.93, 2.57) * mm});
            skLineSegment(sketch, "E64.1.0.2", {"start": v(19.93, 2.57) * mm, "end": v(19.93, 1.93) * mm});
            skLineSegment(sketch, "E64.1.0.3", {"start": v(20.57, 1.93) * mm, "end": v(19.93, 1.93) * mm});
            skPoint(sketch, "E65", {"position": v(20.25, 2.25) * mm});
            skLineSegment(sketch, "E66", {"start": v(19, 2.25) * mm, "end": v(20.25, 2.25) * mm, "construction": true});
            skLineSegment(sketch, "E67", {"start": v(20.25, 2.25) * mm, "end": v(21.5, 2.25) * mm, "construction": true});
            skLineSegment(sketch, "E68", {"start": v(20.25, 3.5) * mm, "end": v(20.25, 2.25) * mm, "construction": true});
            skPoint(sketch, "E68.startSnap0", {"position": v(20.25, 2.57) * mm});
            skLineSegment(sketch, "E69", {"start": v(20.25, 1.17) * mm, "end": v(20.25, 2.25) * mm, "construction": true});
            skPoint(sketch, "E70", {"position": v(21.5, 0) * mm});
            skPoint(sketch, "E71.0.1.0", {"position": v(20.25, 0) * mm});
            skLineSegment(sketch, "E71.0.1.1", {"start": v(20.57, 0.32) * mm, "end": v(20.57, -0.32) * mm});
            skLineSegment(sketch, "E71.0.1.2", {"start": v(20.57, 0.32) * mm, "end": v(19.93, 0.32) * mm});
            skLineSegment(sketch, "E71.0.1.3", {"start": v(19.93, 0.32) * mm, "end": v(19.93, -0.32) * mm});
            skLineSegment(sketch, "E71.0.1.4", {"start": v(20.57, -0.32) * mm, "end": v(19.93, -0.32) * mm});
            skLineSegment(sketch, "E71.0.1.5", {"start": v(18.07, 0.32) * mm, "end": v(18.07, -0.32) * mm});
            skLineSegment(sketch, "E71.0.1.6", {"start": v(18.07, -0.32) * mm, "end": v(17.43, -0.32) * mm});
            skLineSegment(sketch, "E71.0.1.7", {"start": v(17.43, 0.32) * mm, "end": v(17.43, -0.32) * mm});
            skLineSegment(sketch, "E71.0.1.8", {"start": v(18.07, 0.32) * mm, "end": v(17.43, 0.32) * mm});
            skPoint(sketch, "E71.0.2.0", {"position": v(20.25, -2.25) * mm});
            skLineSegment(sketch, "E71.0.2.1", {"start": v(20.57, -1.93) * mm, "end": v(20.57, -2.57) * mm});
            skLineSegment(sketch, "E71.0.2.2", {"start": v(20.57, -1.93) * mm, "end": v(19.93, -1.93) * mm});
            skLineSegment(sketch, "E71.0.2.3", {"start": v(19.93, -1.93) * mm, "end": v(19.93, -2.57) * mm});
            skLineSegment(sketch, "E71.0.2.4", {"start": v(20.57, -2.57) * mm, "end": v(19.93, -2.57) * mm});
            skLineSegment(sketch, "E71.0.2.5", {"start": v(18.07, -1.93) * mm, "end": v(18.07, -2.57) * mm});
            skLineSegment(sketch, "E71.0.2.6", {"start": v(18.07, -2.57) * mm, "end": v(17.43, -2.57) * mm});
            skLineSegment(sketch, "E71.0.2.7", {"start": v(17.43, -1.93) * mm, "end": v(17.43, -2.57) * mm});
            skLineSegment(sketch, "E71.0.2.8", {"start": v(18.07, -1.93) * mm, "end": v(17.43, -1.93) * mm});
            skLineSegment(sketch, "E71.direction1", {"start": v(20.25, 2.25) * mm, "end": v(31.55, 2.25) * mm, "construction": true});
            skLineSegment(sketch, "E71.direction2", {"start": v(20.25, 2.25) * mm, "end": v(20.25, 0) * mm, "construction": true});
            skSolve(sketch);
        }
        {
            var Q0;
            Q0=makeQuery(id+"F11.imprint","IMPRINT",FACE,{"disambiguationData":[TD([[makeQuery(id+"F11.imprint","IMPRINT",EDGE,{"derivedFrom":sQuery(id+"F11.wireOp",EDGE,"E71.0.2.1")}),-1.0]])]});
            var Q1;
            Q1=makeQuery(id+"F11.imprint","IMPRINT",FACE,{"disambiguationData":[TD([[makeQuery(id+"F11.imprint","IMPRINT",EDGE,{"derivedFrom":sQuery(id+"F11.wireOp",EDGE,"E71.0.2.5")}),-1.0]])]});
            var Q2;
            Q2=makeQuery(id+"F11.imprint","IMPRINT",FACE,{"disambiguationData":[TD([[makeQuery(id+"F11.imprint","IMPRINT",EDGE,{"derivedFrom":sQuery(id+"F11.wireOp",EDGE,"E71.0.1.5")}),-1.0]])]});
            var Q3;
            Q3=makeQuery(id+"F11.imprint","IMPRINT",FACE,{"disambiguationData":[TD([[makeQuery(id+"F11.imprint","IMPRINT",EDGE,{"derivedFrom":sQuery(id+"F11.wireOp",EDGE,"E71.0.1.1")}),-1.0]])]});
            var Q4;
            Q4=makeQuery(id+"F11.imprint","IMPRINT",FACE,{"disambiguationData":[TD([[makeQuery(id+"F11.imprint","IMPRINT",EDGE,{"derivedFrom":sQuery(id+"F11.wireOp",EDGE,"E64.1.0.0")}),-1.0]])]});
            var Q5;
            Q5=makeQuery(id+"F11.imprint","IMPRINT",FACE,{"disambiguationData":[TD([[makeQuery(id+"F11.imprint","IMPRINT",EDGE,{"derivedFrom":sQuery(id+"F11.wireOp",EDGE,"E63.bottom")}),1.0]])]});
            extrude(context, id + "F12", {"entities" : qUnion([Q0, Q1, Q2, Q3, Q4, Q5]), "operationType" : NewBodyOperationType.ADD, "depth" : 8 * mm});
        }
        {
            var Q0;
            Q0=makeQuery(id+"F3.opExtrude","SWEPT_EDGE",EDGE,{"disambiguationData":[OSD([sQuery(id+"F0.wireOp",EDGE,"E0.left"),sQuery(id+"F0.wireOp",EDGE,"E7.bottom"),sQuery(id+"F0.wireOp",EDGE,"E7.left")])]});
            var Q1;
            Q1=makeQuery(id+"F3.opExtrude","SWEPT_EDGE",EDGE,{"disambiguationData":[OSD([sQuery(id+"F0.wireOp",EDGE,"E7.bottom"),sQuery(id+"F0.wireOp",EDGE,"E7.right")])]});
            var Q2;
            Q2=makeQuery(id+"F3.opExtrude","SWEPT_EDGE",EDGE,{"disambiguationData":[OSD([sQuery(id+"F0.wireOp",EDGE,"E0.left"),sQuery(id+"F0.wireOp",EDGE,"E7.top"),sQuery(id+"F0.wireOp",EDGE,"E7.left")])]});
            var Q3;
            Q3=makeQuery(id+"F3.opExtrude","SWEPT_EDGE",EDGE,{"disambiguationData":[OSD([sQuery(id+"F0.wireOp",EDGE,"E7.top"),sQuery(id+"F0.wireOp",EDGE,"E7.right")])]});
            chamfer(context, id + "F13", {"entities" : qUnion([Q0, Q1, Q2, Q3]), "width" : 0.4 * mm, "tangentPropagation" : true});
        }
    });
